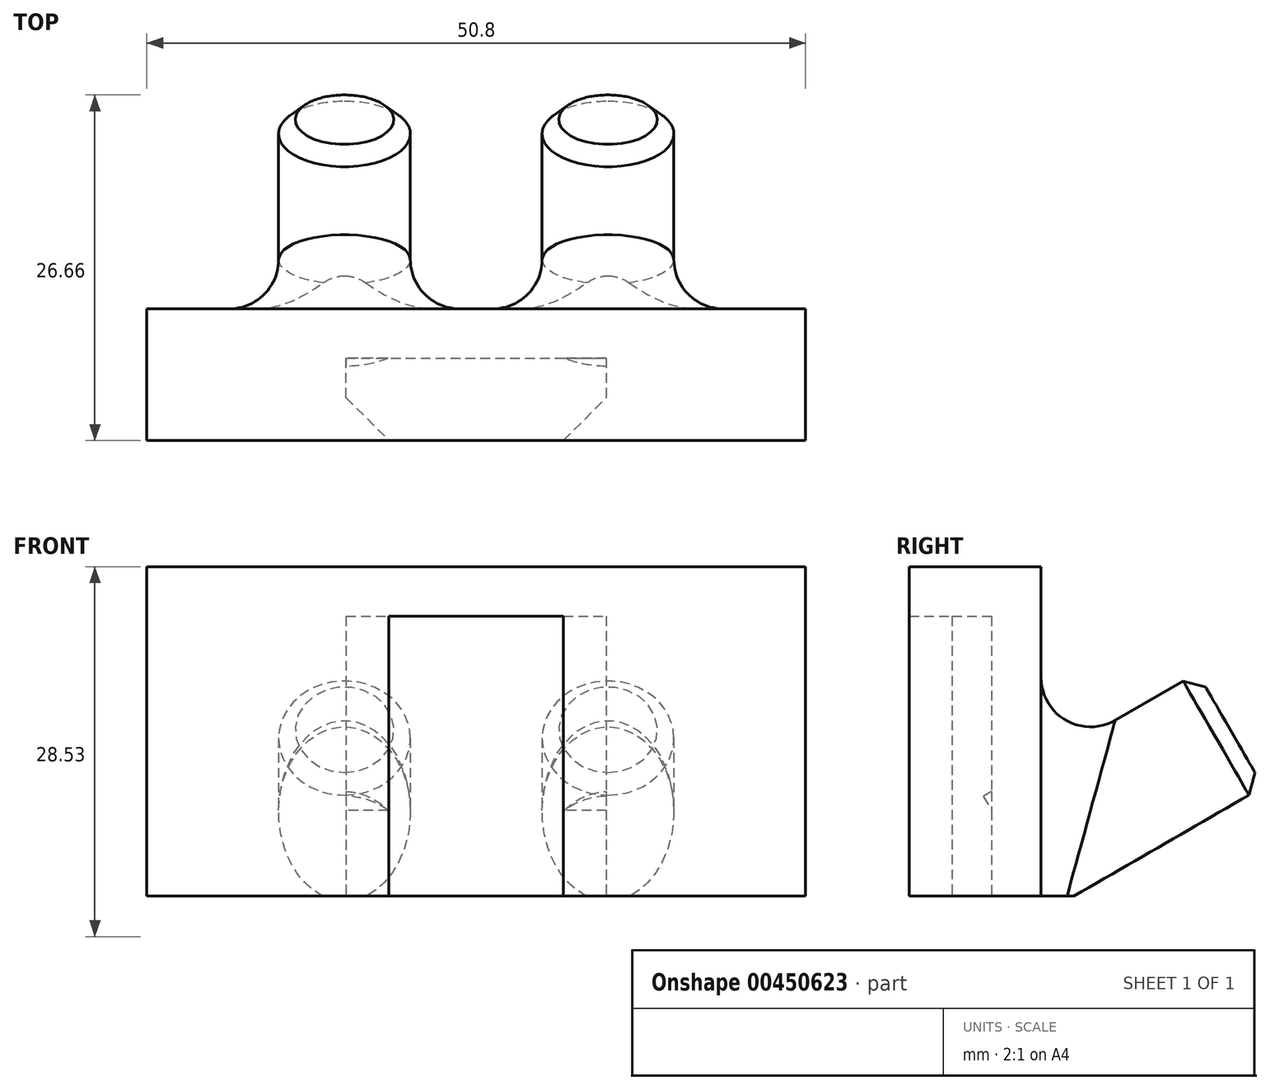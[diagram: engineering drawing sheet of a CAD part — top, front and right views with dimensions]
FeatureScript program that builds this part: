
annotation { "Feature Type Name" : "Feature", "Feature Type Description" : "" }
export const myFeature = defineFeature(function(context is Context, id is Id, definition is map)
    precondition{}
    {
        {
            var Q0;
            Q0=qCreatedBy(makeId("Top.planeOp"),FACE);
            var sketch = newSketch(context, id + "F0", { "sketchPlane" : qUnion([Q0])});
            skLineSegment(sketch, "E0", {"start": v(-6.73, 0) * mm, "end": v(-10.03, 3.3) * mm});
            skLineSegment(sketch, "E1", {"start": v(-10.03, 6.35) * mm, "end": v(10.03, 6.35) * mm});
            skLineSegment(sketch, "E2", {"start": v(10.03, 3.3) * mm, "end": v(6.73, 0) * mm});
            skLineSegment(sketch, "E3", {"start": v(6.73, 0) * mm, "end": v(25.4, 0) * mm});
            skLineSegment(sketch, "E4", {"start": v(25.4, 0) * mm, "end": v(25.4, 10.16) * mm});
            skLineSegment(sketch, "E5", {"start": v(25.4, 10.16) * mm, "end": v(-25.4, 10.16) * mm});
            skLineSegment(sketch, "E6", {"start": v(-25.4, 10.16) * mm, "end": v(-25.4, 0) * mm});
            skLineSegment(sketch, "E7", {"start": v(-25.4, 0) * mm, "end": v(-6.73, 0) * mm});
            skLineSegment(sketch, "E8", {"start": v(10.03, 6.35) * mm, "end": v(10.03, 3.3) * mm});
            skLineSegment(sketch, "E9", {"start": v(-10.03, 6.35) * mm, "end": v(-10.03, 3.3) * mm});
            skSolve(sketch);
        }
        {
            var Q0;
            Q0 = qSketchRegion(id + "F0", true);
            extrude(context, id + "F1", {"entities" : qUnion([Q0]), "depth" : 25.4 * mm});
        }
        {
            var Q0;
            Q0=qCreatedBy(makeId("Front.planeOp"),FACE);
            var sketch = newSketch(context, id + "F2", { "sketchPlane" : qUnion([Q0])});
            skLineSegment(sketch, "E10.bottom", {"start": v(-25.4, 25.4) * mm, "end": v(25.4, 25.4) * mm});
            skLineSegment(sketch, "E10.top", {"start": v(-25.4, 21.59) * mm, "end": v(25.4, 21.59) * mm});
            skLineSegment(sketch, "E10.left", {"start": v(-25.4, 25.4) * mm, "end": v(-25.4, 21.59) * mm});
            skLineSegment(sketch, "E10.right", {"start": v(25.4, 25.4) * mm, "end": v(25.4, 21.59) * mm});
            skSolve(sketch);
        }
        {
            var Q0;
            Q0 = qSketchRegion(id + "F2", true);
            extrude(context, id + "F3", {"entities" : qUnion([Q0]), "operationType" : NewBodyOperationType.ADD, "oppositeDirection" : true, "depth" : 7.62 * mm});
        }
        {
            var Q0;
            Q0=makeQuery(id+"F1.opExtrude","CAP_EDGE",EDGE,{"disambiguationData":[OSD([sQuery(id+"F0.wireOp",EDGE,"E5")])],"isStart":true});
            cPlane(context, id + "F4", {"entities" : qUnion([Q0]), "cplaneType" : CPlaneType.LINE_ANGLE, "offset" : 25.4 * mm, "angle" : 330 * degree, "width" : 152.4 * mm, "height" : 152.4 * mm});
        }
        {
            var Q0;
            Q0=qCreatedBy(id+"F4.planeOp",FACE);
            var sketch = newSketch(context, id + "F5", { "sketchPlane" : qUnion([Q0])});
            skCircle(sketch, "E11", {"center": v(10.16, -1.27) * mm, "radius": 5.08 * mm});
            skCircle(sketch, "E12", {"center": v(-10.16, -1.27) * mm, "radius": 5.08 * mm});
            skSolve(sketch);
        }
        {
            var Q0;
            Q0 = qSketchRegion(id + "F5", true);
            extrude(context, id + "F6", {"entities" : qUnion([Q0]), "operationType" : NewBodyOperationType.ADD, "oppositeDirection" : true, "depth" : 19.05 * mm});
        }
        {
            var Q0;
            Q0=qCreatedBy(makeId("Front.planeOp"),FACE);
            var sketch = newSketch(context, id + "F7", { "sketchPlane" : qUnion([Q0])});
            skLineSegment(sketch, "E13.bottom", {"start": v(-25.34, 0) * mm, "end": v(24.98, 0) * mm});
            skLineSegment(sketch, "E13.top", {"start": v(-25.34, -8.69) * mm, "end": v(24.98, -8.69) * mm});
            skLineSegment(sketch, "E13.left", {"start": v(-25.34, 0) * mm, "end": v(-25.34, -8.69) * mm});
            skLineSegment(sketch, "E13.right", {"start": v(24.98, 0) * mm, "end": v(24.98, -8.69) * mm});
            skSolve(sketch);
        }
        {
            var Q0;
            Q0 = qSketchRegion(id + "F7", true);
            extrude(context, id + "F8", {"entities" : qUnion([Q0]), "operationType" : NewBodyOperationType.REMOVE, "oppositeDirection" : true, "depth" : 25.4 * mm});
        }
        {
            var Q0;
            Q0=makeQuery(id+"F6.boolean.opBoolean","INTERSECT",EDGE,{"derivedFrom":[makeQuery(id+"F1.opExtrude","SWEPT_FACE",FACE,{"disambiguationData":[OSD([sQuery(id+"F0.wireOp",EDGE,"E5")])]}),makeQuery(id+"F6.opExtrude","SWEPT_FACE",FACE,{"disambiguationData":[OSD([sQuery(id+"F5.wireOp",EDGE,"E11")])]})]});
            var Q1;
            Q1=makeQuery(id+"F6.boolean.opBoolean","INTERSECT",EDGE,{"derivedFrom":[makeQuery(id+"F1.opExtrude","SWEPT_FACE",FACE,{"disambiguationData":[OSD([sQuery(id+"F0.wireOp",EDGE,"E5")])]}),makeQuery(id+"F6.opExtrude","SWEPT_FACE",FACE,{"disambiguationData":[OSD([sQuery(id+"F5.wireOp",EDGE,"E12")])]})]});
            fillet(context, id + "F9", {"entities" : qUnion([Q0, Q1]), "radius" : 3.8 * mm, "tangentPropagation" : true, "allowEdgeOverflow" : false});
        }
        {
            var Q0;
            Q0=makeQuery(id+"F6.opExtrude","CAP_EDGE",EDGE,{"disambiguationData":[OSD([sQuery(id+"F5.wireOp",EDGE,"E12")])],"isStart":false});
            var Q1;
            Q1=makeQuery(id+"F6.opExtrude","CAP_EDGE",EDGE,{"disambiguationData":[OSD([sQuery(id+"F5.wireOp",EDGE,"E11")])],"isStart":false});
            chamfer(context, id + "F10", {"entities" : qUnion([Q0, Q1]), "width" : 1.27 * mm, "tangentPropagation" : true});
        }
    });
